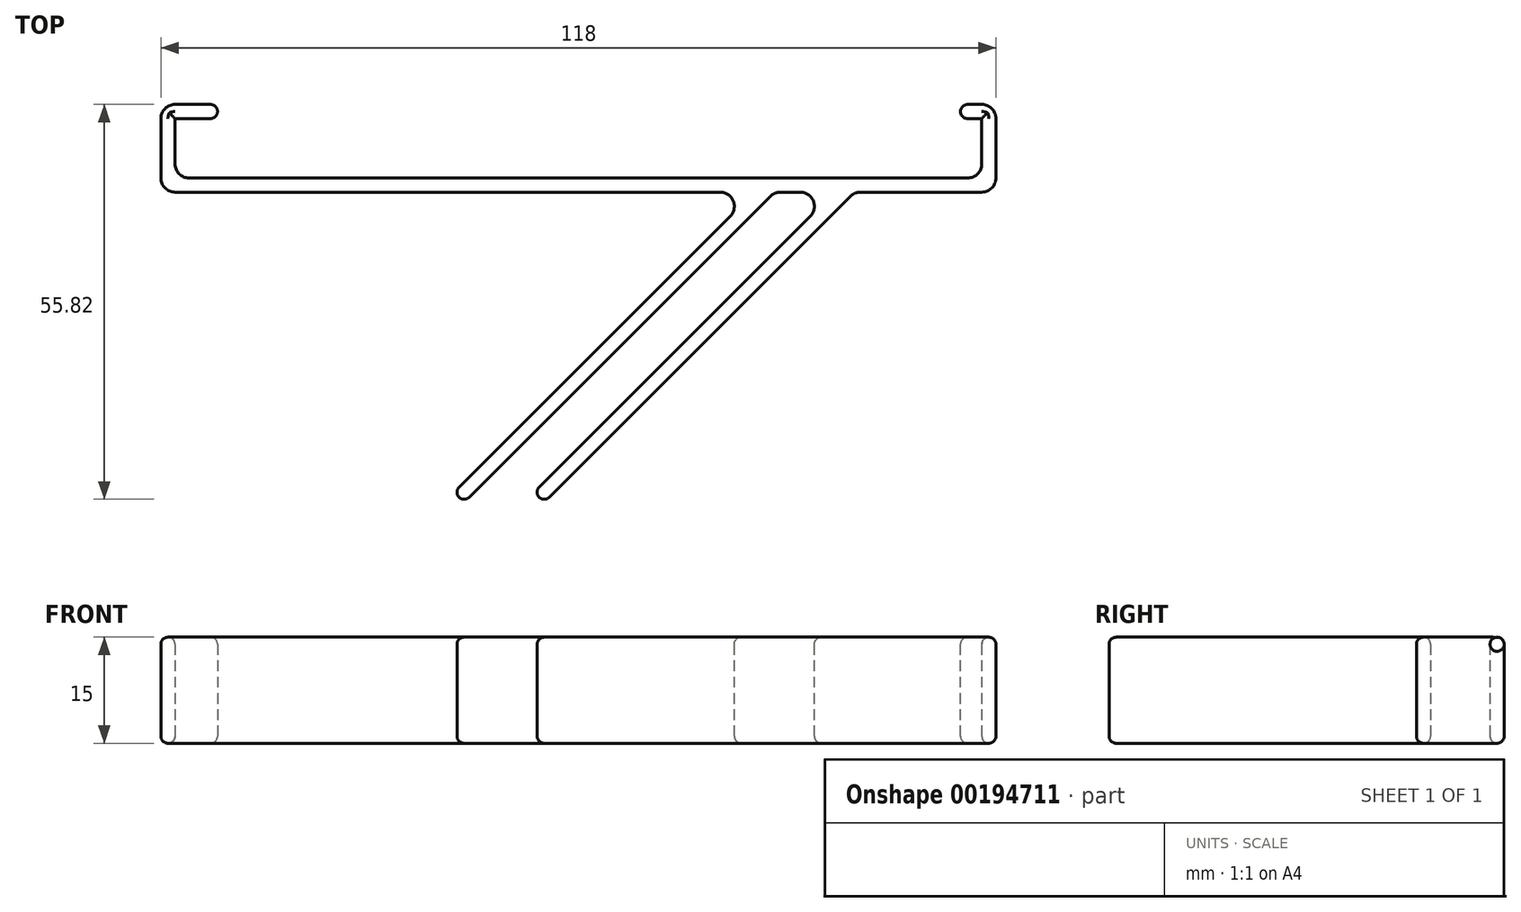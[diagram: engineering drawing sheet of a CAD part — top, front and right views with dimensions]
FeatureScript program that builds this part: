
annotation { "Feature Type Name" : "Feature", "Feature Type Description" : "" }
export const myFeature = defineFeature(function(context is Context, id is Id, definition is map)
    precondition{}
    {
        {
            var Q0;
            Q0=qCreatedBy(makeId("Top.planeOp"),FACE);
            var sketch = newSketch(context, id + "F0", { "sketchPlane" : qUnion([Q0])});
            skLineSegment(sketch, "E0.bottom", {"start": v(-52.04, 0.3) * mm, "end": v(61.96, 0.3) * mm});
            skLineSegment(sketch, "E0.top", {"start": v(-52.04, -1.7) * mm, "end": v(61.96, -1.7) * mm});
            skLineSegment(sketch, "E0.left", {"start": v(-52.04, 0.3) * mm, "end": v(-52.04, -1.7) * mm});
            skLineSegment(sketch, "E0.right", {"start": v(61.96, 0.3) * mm, "end": v(61.96, -1.7) * mm});
            skLineSegment(sketch, "E1.bottom", {"start": v(-52.04, -1.7) * mm, "end": v(-54.04, -1.7) * mm});
            skLineSegment(sketch, "E1.top", {"start": v(-52.04, 8.7) * mm, "end": v(-54.04, 8.7) * mm});
            skLineSegment(sketch, "E1.left", {"start": v(-52.04, -1.7) * mm, "end": v(-52.04, 8.7) * mm});
            skLineSegment(sketch, "E1.right", {"start": v(-54.04, -1.7) * mm, "end": v(-54.04, 8.7) * mm});
            skLineSegment(sketch, "E2.bottom", {"start": v(61.96, -1.7) * mm, "end": v(63.96, -1.7) * mm});
            skLineSegment(sketch, "E2.top", {"start": v(61.96, 8.7) * mm, "end": v(63.96, 8.7) * mm});
            skLineSegment(sketch, "E2.left", {"start": v(61.96, -1.7) * mm, "end": v(61.96, 8.7) * mm});
            skLineSegment(sketch, "E2.right", {"start": v(63.96, -1.7) * mm, "end": v(63.96, 8.7) * mm});
            skLineSegment(sketch, "E3.bottom", {"start": v(-54.04, 8.7) * mm, "end": v(-46.04, 8.7) * mm});
            skLineSegment(sketch, "E3.top", {"start": v(-54.04, 10.7) * mm, "end": v(-46.04, 10.7) * mm});
            skLineSegment(sketch, "E3.left", {"start": v(-54.04, 8.7) * mm, "end": v(-54.04, 10.7) * mm});
            skLineSegment(sketch, "E3.right", {"start": v(-46.04, 8.7) * mm, "end": v(-46.04, 10.7) * mm});
            skLineSegment(sketch, "E4.bottom", {"start": v(63.96, 8.7) * mm, "end": v(58.96, 8.7) * mm});
            skLineSegment(sketch, "E4.top", {"start": v(63.96, 10.7) * mm, "end": v(58.96, 10.7) * mm});
            skLineSegment(sketch, "E4.left", {"start": v(63.96, 8.7) * mm, "end": v(63.96, 10.7) * mm});
            skLineSegment(sketch, "E4.right", {"start": v(58.96, 8.7) * mm, "end": v(58.96, 10.7) * mm});
            skLineSegment(sketch, "E5", {"start": v(41.14, -1.7) * mm, "end": v(-1.29, -44.12) * mm});
            skLineSegment(sketch, "E6", {"start": v(0.12, -45.54) * mm, "end": v(43.96, -1.7) * mm});
            skLineSegment(sketch, "E7", {"start": v(0.12, -45.54) * mm, "end": v(-1.29, -44.12) * mm});
            skLineSegment(sketch, "E8", {"start": v(32.65, -1.7) * mm, "end": v(-11.19, -45.54) * mm});
            skLineSegment(sketch, "E9", {"start": v(-11.19, -45.54) * mm, "end": v(-12.6, -44.12) * mm});
            skLineSegment(sketch, "E10", {"start": v(-12.6, -44.12) * mm, "end": v(29.82, -1.7) * mm});
            skSolve(sketch);
        }
        {
            var Q0;
            Q0=qSketchRegion(id+"F0",true);
            extrude(context, id + "F1", {"entities" : qUnion([Q0]), "depth" : 15 * mm});
        }
        {
            var Q0;
            Q0=makeQuery(id+"F1.opExtrude","SWEPT_EDGE",EDGE,{"disambiguationData":[OSD([sQuery(id+"F0.wireOp",EDGE,"E4.top"),sQuery(id+"F0.wireOp",EDGE,"E4.right")])]});
            var Q1;
            Q1=makeQuery(id+"F1.opExtrude","SWEPT_EDGE",EDGE,{"disambiguationData":[OSD([sQuery(id+"F0.wireOp",EDGE,"E4.bottom"),sQuery(id+"F0.wireOp",EDGE,"E4.right")])]});
            var Q2;
            Q2=makeQuery(id+"F1.opExtrude","SWEPT_EDGE",EDGE,{"disambiguationData":[OSD([sQuery(id+"F0.wireOp",EDGE,"E3.bottom"),sQuery(id+"F0.wireOp",EDGE,"E3.right")])]});
            var Q3;
            Q3=makeQuery(id+"F1.opExtrude","SWEPT_EDGE",EDGE,{"disambiguationData":[OSD([sQuery(id+"F0.wireOp",EDGE,"E3.top"),sQuery(id+"F0.wireOp",EDGE,"E3.right")])]});
            var Q4;
            Q4=makeQuery(id+"F1.opExtrude","SWEPT_EDGE",EDGE,{"disambiguationData":[OSD([sQuery(id+"F0.wireOp",EDGE,"cbmLmww0-s3Uw-X8MJ-5Prn-tQJUQLKUa4ud.bottom"),sQuery(id+"F0.wireOp",EDGE,"cbmLmww0-s3Uw-X8MJ-5Prn-tQJUQLKUa4ud.right")])]});
            var Q5;
            Q5=makeQuery(id+"F1.opExtrude","SWEPT_EDGE",EDGE,{"disambiguationData":[OSD([sQuery(id+"F0.wireOp",EDGE,"cbmLmww0-s3Uw-X8MJ-5Prn-tQJUQLKUa4ud.top"),sQuery(id+"F0.wireOp",EDGE,"cbmLmww0-s3Uw-X8MJ-5Prn-tQJUQLKUa4ud.right")])]});
            var Q6;
            Q6=makeQuery(id+"F1.opExtrude","SWEPT_EDGE",EDGE,{"disambiguationData":[OSD([sQuery(id+"F0.wireOp",EDGE,"E6"),sQuery(id+"F0.wireOp",EDGE,"E7")])]});
            var Q7;
            Q7=makeQuery(id+"F1.opExtrude","SWEPT_EDGE",EDGE,{"disambiguationData":[OSD([sQuery(id+"F0.wireOp",EDGE,"E5"),sQuery(id+"F0.wireOp",EDGE,"E7")])]});
            var Q8;
            Q8=makeQuery(id+"F1.opExtrude","SWEPT_EDGE",EDGE,{"disambiguationData":[OSD([sQuery(id+"F0.wireOp",EDGE,"E8"),sQuery(id+"F0.wireOp",EDGE,"E9")])]});
            var Q9;
            Q9=makeQuery(id+"F1.opExtrude","SWEPT_EDGE",EDGE,{"disambiguationData":[OSD([sQuery(id+"F0.wireOp",EDGE,"E9"),sQuery(id+"F0.wireOp",EDGE,"E10")])]});
            fillet(context, id + "F2", {"entities" : qUnion([Q0, Q1, Q2, Q3, Q4, Q5, Q6, Q7, Q8, Q9]), "radius" : 1 * mm, "tangentPropagation" : true, "allowEdgeOverflow" : false});
        }
        {
            var Q0;
            Q0=makeQuery(id+"F1.opExtrude","SWEPT_EDGE",EDGE,{"disambiguationData":[OSD([sQuery(id+"F0.wireOp",EDGE,"E3.top"),sQuery(id+"F0.wireOp",EDGE,"E3.left")])]});
            var Q1;
            Q1=makeQuery(id+"F1.opExtrude","SWEPT_EDGE",EDGE,{"disambiguationData":[OSD([sQuery(id+"F0.wireOp",EDGE,"E1.bottom"),sQuery(id+"F0.wireOp",EDGE,"E1.right")])]});
            var Q2;
            Q2=makeQuery(id+"F1.opExtrude","SWEPT_EDGE",EDGE,{"disambiguationData":[OSD([sQuery(id+"F0.wireOp",EDGE,"E2.bottom"),sQuery(id+"F0.wireOp",EDGE,"E2.right")])]});
            var Q3;
            Q3=makeQuery(id+"F1.opExtrude","SWEPT_EDGE",EDGE,{"disambiguationData":[OSD([sQuery(id+"F0.wireOp",EDGE,"E4.top"),sQuery(id+"F0.wireOp",EDGE,"E4.left")])]});
            var Q4;
            Q4=makeQuery(id+"F1.opExtrude","SWEPT_EDGE",EDGE,{"disambiguationData":[OSD([sQuery(id+"F0.wireOp",EDGE,"cbmLmww0-s3Uw-X8MJ-5Prn-tQJUQLKUa4ud.top"),sQuery(id+"F0.wireOp",EDGE,"cbmLmww0-s3Uw-X8MJ-5Prn-tQJUQLKUa4ud.left")])]});
            var Q5;
            Q5=makeQuery(id+"F1.opExtrude","SWEPT_EDGE",EDGE,{"disambiguationData":[OSD([sQuery(id+"F0.wireOp",EDGE,"E0.top"),sQuery(id+"F0.wireOp",EDGE,"DhNBHtjC-mmht-2zA3-qtbX-Vav0KUQkQ3ZT.bottom"),sQuery(id+"F0.wireOp",EDGE,"DhNBHtjC-mmht-2zA3-qtbX-Vav0KUQkQ3ZT.right")])]});
            var Q6;
            Q6=makeQuery(id+"F1.opExtrude","SWEPT_EDGE",EDGE,{"disambiguationData":[OSD([sQuery(id+"F0.wireOp",EDGE,"E0.top"),sQuery(id+"F0.wireOp",EDGE,"DhNBHtjC-mmht-2zA3-qtbX-Vav0KUQkQ3ZT.bottom"),sQuery(id+"F0.wireOp",EDGE,"DhNBHtjC-mmht-2zA3-qtbX-Vav0KUQkQ3ZT.left")])]});
            var Q7;
            Q7=makeQuery(id+"F1.opExtrude","SWEPT_EDGE",EDGE,{"disambiguationData":[OSD([sQuery(id+"F0.wireOp",EDGE,"DhNBHtjC-mmht-2zA3-qtbX-Vav0KUQkQ3ZT.right"),sQuery(id+"F0.wireOp",EDGE,"cbmLmww0-s3Uw-X8MJ-5Prn-tQJUQLKUa4ud.bottom")])]});
            var Q8;
            Q8=makeQuery(id+"F1.opExtrude","SWEPT_EDGE",EDGE,{"disambiguationData":[OSD([sQuery(id+"F0.wireOp",EDGE,"E0.bottom"),sQuery(id+"F0.wireOp",EDGE,"E1.left")])]});
            var Q9;
            Q9=makeQuery(id+"F1.opExtrude","SWEPT_EDGE",EDGE,{"disambiguationData":[OSD([sQuery(id+"F0.wireOp",EDGE,"E0.bottom"),sQuery(id+"F0.wireOp",EDGE,"E2.left")])]});
            fillet(context, id + "F3", {"entities" : qUnion([Q0, Q1, Q2, Q3, Q4, Q5, Q6, Q7, Q8, Q9]), "radius" : 2 * mm, "tangentPropagation" : true, "allowEdgeOverflow" : false});
        }
        {
            var Q0;
            Q0=makeQuery(id+"F1.opExtrude","CAP_EDGE",EDGE,{"disambiguationData":[OSD([sQuery(id+"F0.wireOp",EDGE,"E6")])],"isStart":false});
            var Q1;
            Q1=makeQuery(id+"F1.opExtrude","CAP_EDGE",EDGE,{"disambiguationData":[OSD([sQuery(id+"F0.wireOp",EDGE,"E0.bottom")])],"isStart":false});
            var Q2;
            Q2=makeQuery(id+"F1.opExtrude","CAP_EDGE",EDGE,{"disambiguationData":[OSD([sQuery(id+"F0.wireOp",EDGE,"E5")])],"isStart":true});
            var Q3;
            Q3=makeQuery(id+"F1.opExtrude","CAP_EDGE",EDGE,{"disambiguationData":[OSD([sQuery(id+"F0.wireOp",EDGE,"E0.bottom")])],"isStart":true});
            fillet(context, id + "F4", {"entities" : qUnion([Q0, Q1, Q2, Q3]), "radius" : 1 * mm, "tangentPropagation" : true, "allowEdgeOverflow" : false});
        }
    });
